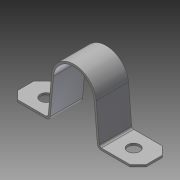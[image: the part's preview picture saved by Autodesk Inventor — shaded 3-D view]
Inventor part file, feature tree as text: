
AUTODESK INVENTOR PART (.ipt)
format: ipt  version: 2014 SP1 (Build 180222100, 222)  size: 133,120 bytes
history: native  units: in
note: dims shown in document units (in); Inventor stores cm internally (conversion verified against a paired STEP export)
features: extrude x2, sketch x2, chamfer x1, projected_geometry x1
ambient origin geometry x8: Origin, YZ Plane, XZ Plane, XY Plane, X Axis, Y Axis, Z Axis, Center Point
bodies: Solid1 (feature_tree)
feature tree (6):
  extrude  "Extrusion1"  Depth=0.625in
  chamfer  "Chamfer1"  Distance=0.6528in
  extrude  "Extrusion2"  Depth=0.5in
  sketch  "Sketch1"  dims[d0=0.625in d1=0.625in]
  sketch  "Sketch2"  dims[d2=0.0625in d3=0.6528in d4=0.6528in d6=0.0312in d7=0.5in d8=0.0in d9=0.125in d10=0.125in d11=45.0deg d12=0.1875in d13=0.1875in d14=0.25in d15=0.25in d16=0.5in d17=0.0in d18=0.575in d19=0.7255in]
  projected_geometry  "Projected Loop1"
